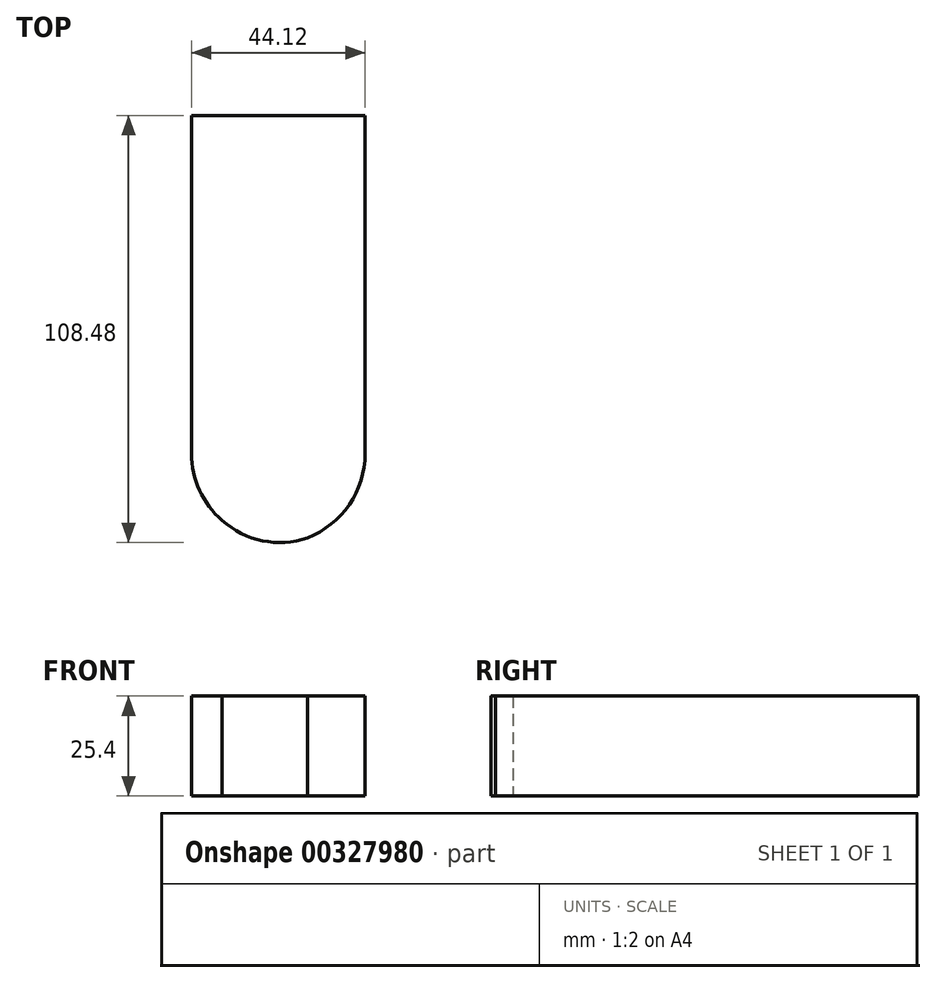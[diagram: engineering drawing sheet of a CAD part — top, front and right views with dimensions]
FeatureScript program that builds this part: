
annotation { "Feature Type Name" : "Feature", "Feature Type Description" : "" }
export const myFeature = defineFeature(function(context is Context, id is Id, definition is map)
    precondition{}
    {
        {
            var Q0;
            Q0=qCreatedBy(makeId("Top.planeOp"),FACE);
            var sketch = newSketch(context, id + "F0", { "sketchPlane" : qUnion([Q0])});
            skLineSegment(sketch, "E0", {"start": v(-26.63, 31.72) * mm, "end": v(17.49, 31.72) * mm});
            skLineSegment(sketch, "E1", {"start": v(17.49, 31.72) * mm, "end": v(17.49, -54.17) * mm});
            skPoint(sketch, "E2.visualSharp", {"position": v(-26.63, -54.17) * mm});
            skLineSegment(sketch, "E3", {"start": v(-26.63, 31.72) * mm, "end": v(-26.63, -54.17) * mm});
            skArc(sketch, "E4", {"start": v(2.87, -75.57) * mm, "mid": v(13.49, -67.13) * mm, "end": v(17.49, -54.17) * mm});
            skArc(sketch, "E5", {"start": v(-18.8, -71.13) * mm, "mid": v(-8.57, -76.32) * mm, "end": v(2.87, -75.57) * mm});
            skArc(sketch, "E6", {"start": v(-26.63, -54.17) * mm, "mid": v(-24.57, -63.51) * mm, "end": v(-18.8, -71.13) * mm});
            skSolve(sketch);
        }
        {
            var Q0;
            Q0=makeQuery(id+"F0.imprint","IMPRINT",FACE,{"disambiguationData":[TD([[makeQuery(id+"F0.imprint","IMPRINT",EDGE,{"derivedFrom":sQuery(id+"F0.wireOp",EDGE,"E0")}),-1.0]])]});
            extrude(context, id + "F1", {"entities" : qUnion([Q0]), "depth" : 25.4 * mm});
        }
    });
